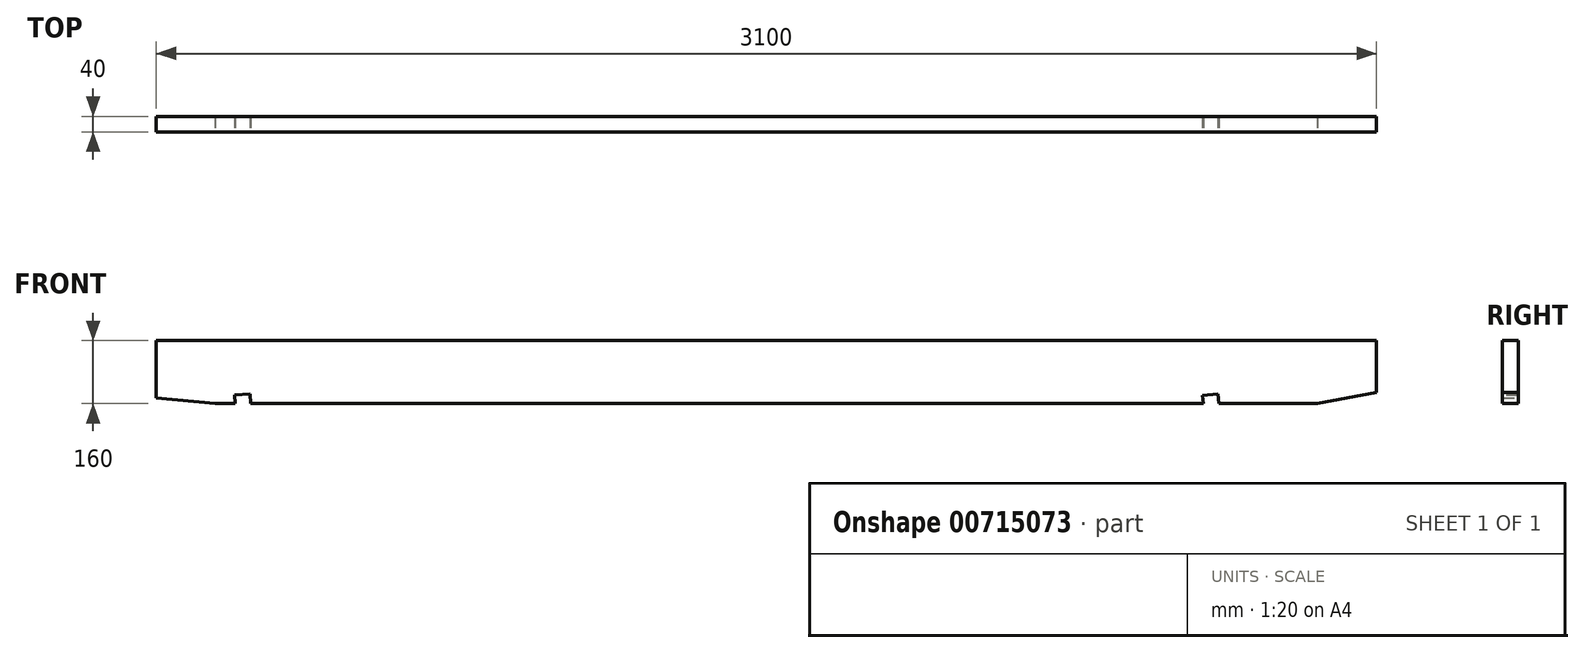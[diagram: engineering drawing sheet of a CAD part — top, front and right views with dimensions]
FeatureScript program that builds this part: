
annotation { "Feature Type Name" : "Feature", "Feature Type Description" : "" }
export const myFeature = defineFeature(function(context is Context, id is Id, definition is map)
    precondition{}
    {
        {
            assignVariable(context, id + "F0", {"name" : "Laenge", "anyValue" : 3100});
        }
        {
            var Q0;
            Q0=qCreatedBy(makeId("Right.planeOp"),FACE);
            var sketch = newSketch(context, id + "F1", { "sketchPlane" : qUnion([Q0])});
            skLineSegment(sketch, "E0.bottom", {"start": v(20, 80) * mm, "end": v(-20, 80) * mm});
            skLineSegment(sketch, "E0.top", {"start": v(20, -80) * mm, "end": v(-20, -80) * mm});
            skLineSegment(sketch, "E0.left", {"start": v(20, 80) * mm, "end": v(20, -80) * mm});
            skLineSegment(sketch, "E0.right", {"start": v(-20, 80) * mm, "end": v(-20, -80) * mm});
            skPoint(sketch, "E0.middle", {"position": v(0, 0) * mm});
            skSolve(sketch);
        }
        {
            var Q0;
            Q0=makeQuery(id+"F1.imprint","IMPRINT",FACE,{"disambiguationData":[TD([[makeQuery(id+"F1.imprint","IMPRINT",EDGE,{"derivedFrom":sQuery(id+"F1.wireOp",EDGE,"E0.bottom")}),1.0]])]});
            extrude(context, id + "F2", {"entities" : qUnion([Q0]), "endBound" : BoundingType.SYMMETRIC, "depth" : (getVariable(context, 'Laenge')) * mm, "offsetDistance" : 25 * mm});
        }
        {
            var Q0;
            Q0=qCreatedBy(makeId("Front.planeOp"),FACE);
            var sketch = newSketch(context, id + "F3", { "sketchPlane" : qUnion([Q0])});
            skLineSegment(sketch, "E1", {"start": v(1823.39, 0) * mm, "end": v(1823.39, -300) * mm});
            skLineSegment(sketch, "E2", {"start": v(1823.39, -300) * mm, "end": v(-2254.27, -300) * mm});
            skLineSegment(sketch, "E3", {"start": v(-2254.27, -300) * mm, "end": v(-2254.27, 0) * mm});
            skLineSegment(sketch, "E4", {"start": v(-2254.27, 0) * mm, "end": v(-1400, -80) * mm});
            skLineSegment(sketch, "E5", {"start": v(-1400, -80) * mm, "end": v(-1400, -180) * mm});
            skLineSegment(sketch, "E6", {"start": v(-1400, -180) * mm, "end": v(1400, -180) * mm});
            skLineSegment(sketch, "E7", {"start": v(1400, -180) * mm, "end": v(1400, -80) * mm});
            skLineSegment(sketch, "E8", {"start": v(1400, -80) * mm, "end": v(1823.39, 0) * mm});
            skLineSegment(sketch, "E9", {"start": v(-1350, -80) * mm, "end": v(-1351.32, -57.38) * mm});
            skLineSegment(sketch, "E10", {"start": v(-1351.32, -57.38) * mm, "end": v(-1311.4, -55.04) * mm});
            skLineSegment(sketch, "E11", {"start": v(-1311.4, -55.04) * mm, "end": v(-1309.93, -80) * mm});
            skLineSegment(sketch, "E12", {"start": v(-1309.93, -80) * mm, "end": v(-1350, -80) * mm});
            skLineSegment(sketch, "E13", {"start": v(1109.82, -80) * mm, "end": v(1107.84, -58.84) * mm});
            skLineSegment(sketch, "E14", {"start": v(1107.84, -58.84) * mm, "end": v(1147.67, -55.1) * mm});
            skLineSegment(sketch, "E15", {"start": v(1147.67, -55.1) * mm, "end": v(1150, -80) * mm});
            skLineSegment(sketch, "E16", {"start": v(1150, -80) * mm, "end": v(1109.82, -80) * mm});
            skSolve(sketch);
        }
        {
            var Q0;
            Q0=makeQuery(id+"F3.imprint","IMPRINT",FACE,{"disambiguationData":[TD([[makeQuery(id+"F3.imprint","IMPRINT",EDGE,{"derivedFrom":sQuery(id+"F3.wireOp",EDGE,"E1")}),-1.0]])]});
            var Q1;
            Q1=makeQuery(id+"F3.imprint","IMPRINT",FACE,{"disambiguationData":[TD([[makeQuery(id+"F3.imprint","IMPRINT",EDGE,{"derivedFrom":sQuery(id+"F3.wireOp",EDGE,"E13")}),-1.0]])]});
            var Q2;
            Q2=makeQuery(id+"F3.imprint","IMPRINT",FACE,{"disambiguationData":[TD([[makeQuery(id+"F3.imprint","IMPRINT",EDGE,{"derivedFrom":sQuery(id+"F3.wireOp",EDGE,"E9")}),-1.0]])]});
            extrude(context, id + "F4", {"entities" : qUnion([Q0, Q1, Q2]), "operationType" : NewBodyOperationType.REMOVE, "endBound" : BoundingType.SYMMETRIC, "oppositeDirection" : true, "depth" : 100 * mm, "offsetDistance" : 25 * mm});
        }
    });
